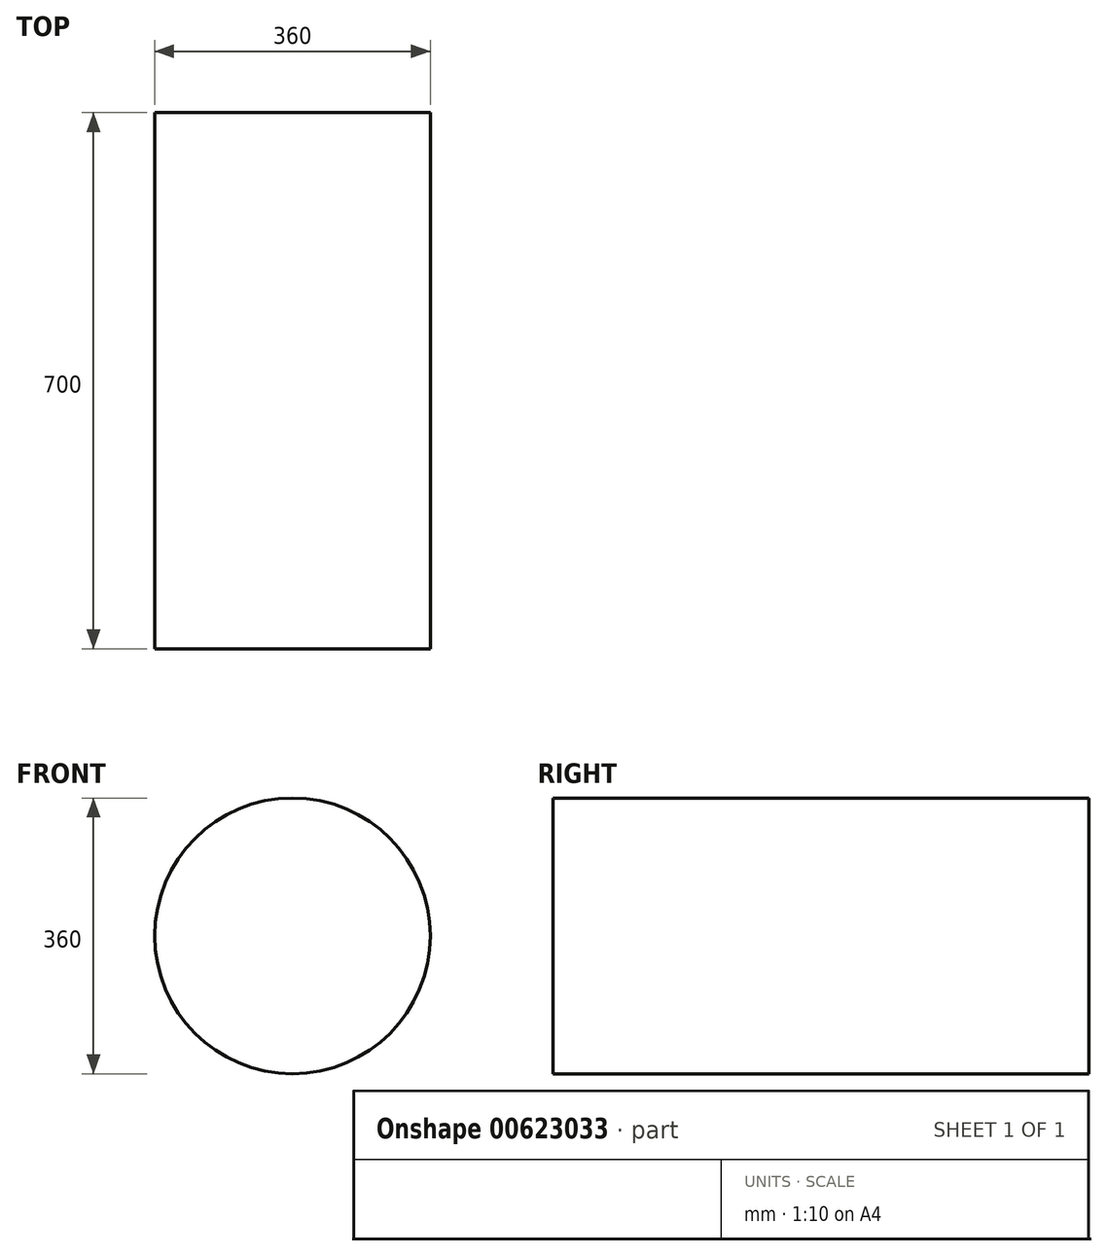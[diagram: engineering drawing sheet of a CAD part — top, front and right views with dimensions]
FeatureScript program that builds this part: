
annotation { "Feature Type Name" : "Feature", "Feature Type Description" : "" }
export const myFeature = defineFeature(function(context is Context, id is Id, definition is map)
    precondition{}
    {
        {
            var Q0;
            Q0=qCreatedBy(makeId("Front.planeOp"),FACE);
            var sketch = newSketch(context, id + "F0", { "sketchPlane" : qUnion([Q0])});
            skCircle(sketch, "E0", {"center": v(0, 0) * mm, "radius": 180 * mm});
            skSolve(sketch);
        }
        {
            var Q0;
            Q0 = qSketchRegion(id + "F0", true);
            extrude(context, id + "F1", {"entities" : qUnion([Q0]), "depth" : 700 * mm, "offsetDistance" : 25 * mm});
        }
    });
